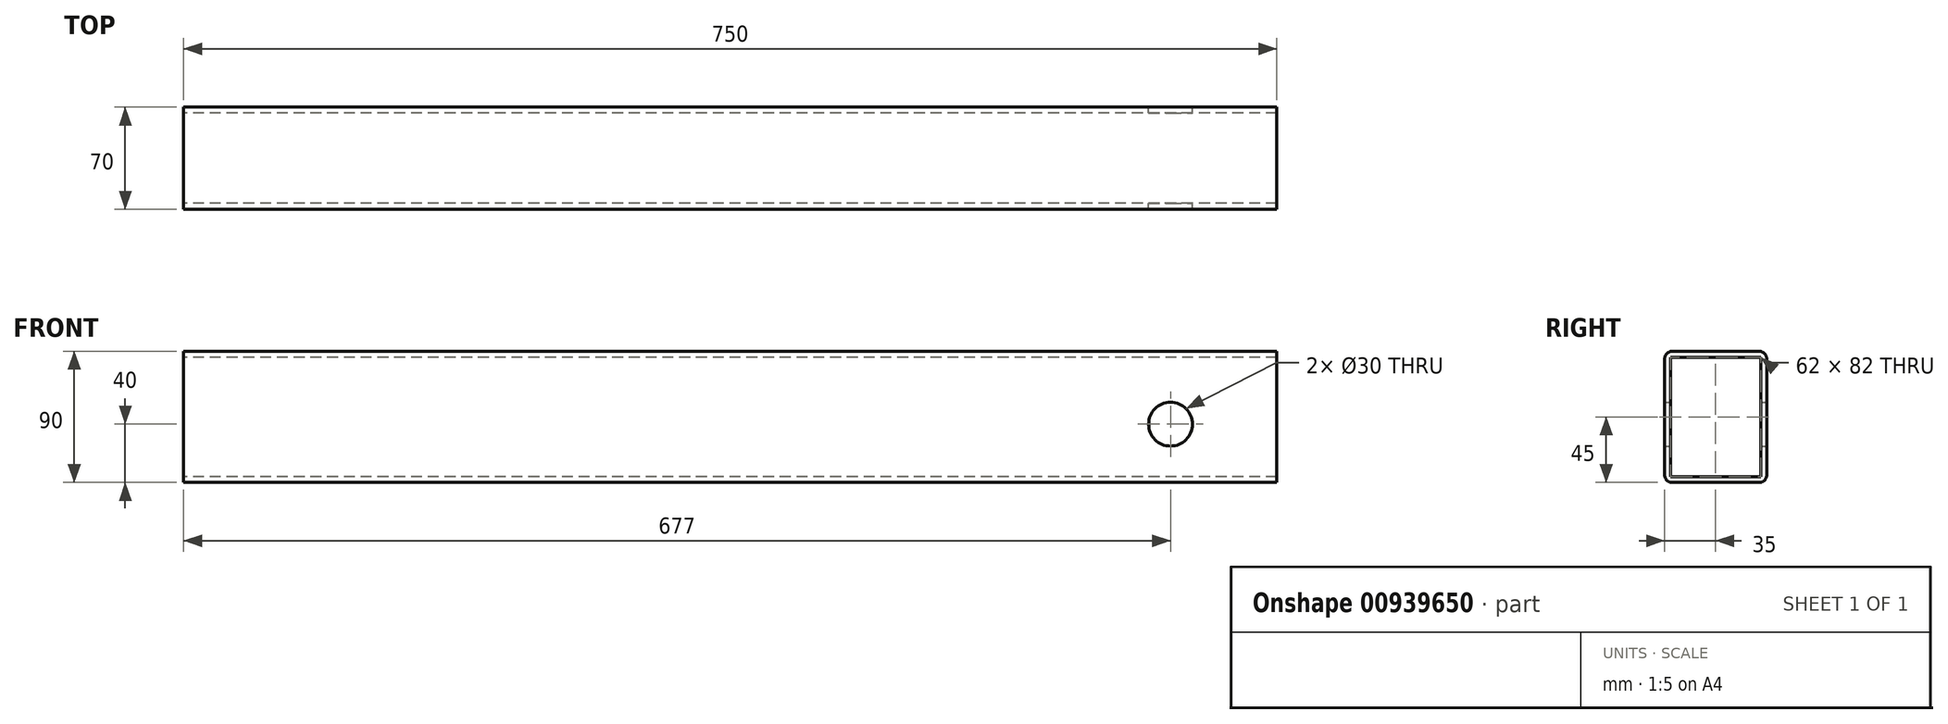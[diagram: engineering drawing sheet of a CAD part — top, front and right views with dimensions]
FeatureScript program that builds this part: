
annotation { "Feature Type Name" : "Feature", "Feature Type Description" : "" }
export const myFeature = defineFeature(function(context is Context, id is Id, definition is map)
    precondition{}
    {
        {
            var Q0;
            Q0=qCreatedBy(makeId("Front.planeOp"),FACE);
            var sketch = newSketch(context, id + "F0", { "sketchPlane" : qUnion([Q0])});
            skLineSegment(sketch, "E0.bottom", {"start": v(375, -45) * mm, "end": v(-375, -45) * mm});
            skLineSegment(sketch, "E0.top", {"start": v(375, 45) * mm, "end": v(-375, 45) * mm});
            skLineSegment(sketch, "E0.left", {"start": v(375, -45) * mm, "end": v(375, 45) * mm});
            skLineSegment(sketch, "E0.right", {"start": v(-375, -45) * mm, "end": v(-375, 45) * mm});
            skPoint(sketch, "E0.middle", {"position": v(0, 0) * mm});
            skPoint(sketch, "E1.visualSharp", {"position": v(-375, 45) * mm});
            skArc(sketch, "E1.filletArc", {"start": v(-375, 45) * mm, "mid": v(-375, 45) * mm, "end": v(-375, 45) * mm});
            skPoint(sketch, "E2.visualSharp", {"position": v(-375, -45) * mm});
            skArc(sketch, "E2.filletArc", {"start": v(-375, -45) * mm, "mid": v(-375, -45) * mm, "end": v(-375, -45) * mm});
            skSolve(sketch);
        }
        {
            var Q0;
            Q0=makeQuery(id+"F0.imprint","IMPRINT",FACE,{"disambiguationData":[TD([[makeQuery(id+"F0.imprint","IMPRINT",EDGE,{"derivedFrom":sQuery(id+"F0.wireOp",EDGE,"E0.bottom")}),-1.0]])]});
            extrude(context, id + "F1", {"entities" : qUnion([Q0]), "depth" : 70 * mm, "offsetDistance" : 25 * mm});
        }
        {
            var Q0;
            Q0=makeQuery(id+"F1.opExtrude","SWEPT_FACE",FACE,{"disambiguationData":[OSD([sQuery(id+"F0.wireOp",EDGE,"E0.right")])]});
            var Q1;
            Q1=makeQuery(id+"F1.opExtrude","SWEPT_FACE",FACE,{"disambiguationData":[OSD([sQuery(id+"F0.wireOp",EDGE,"E0.left")])]});
            shell(context, id + "F2", {"entities" : qUnion([Q0, Q1]), "thickness" : 4 * mm});
        }
        {
            var Q0;
            Q0=makeQuery(id+"F1.opExtrude","CAP_EDGE",EDGE,{"disambiguationData":[OSD([sQuery(id+"F0.wireOp",EDGE,"E0.top")])],"isStart":false});
            var Q1;
            Q1=makeQuery(id+"F1.opExtrude","CAP_EDGE",EDGE,{"disambiguationData":[OSD([sQuery(id+"F0.wireOp",EDGE,"E0.top")])],"isStart":true});
            var Q2;
            Q2=makeQuery(id+"F1.opExtrude","CAP_EDGE",EDGE,{"disambiguationData":[OSD([sQuery(id+"F0.wireOp",EDGE,"E0.bottom")])],"isStart":true});
            var Q3;
            Q3=makeQuery(id+"F1.opExtrude","CAP_EDGE",EDGE,{"disambiguationData":[OSD([sQuery(id+"F0.wireOp",EDGE,"E0.bottom")])],"isStart":false});
            fillet(context, id + "F3", {"entities" : qUnion([Q0, Q1, Q2, Q3]), "radius" : 5 * mm, "tangentPropagation" : true, "allowEdgeOverflow" : false});
        }
        {
            var Q0;
            Q0=qCreatedBy(makeId("Front.planeOp"),FACE);
            var sketch = newSketch(context, id + "F4", { "sketchPlane" : qUnion([Q0])});
            skCircle(sketch, "E3", {"center": v(302, -5) * mm, "radius": 15 * mm});
            skSolve(sketch);
        }
        {
            var Q0;
            Q0 = qSketchRegion(id + "F4", true);
            extrude(context, id + "F5", {"entities" : qUnion([Q0]), "operationType" : NewBodyOperationType.REMOVE, "endBound" : BoundingType.THROUGH_ALL, "depth" : 25 * mm, "offsetDistance" : 25 * mm});
        }
    });
